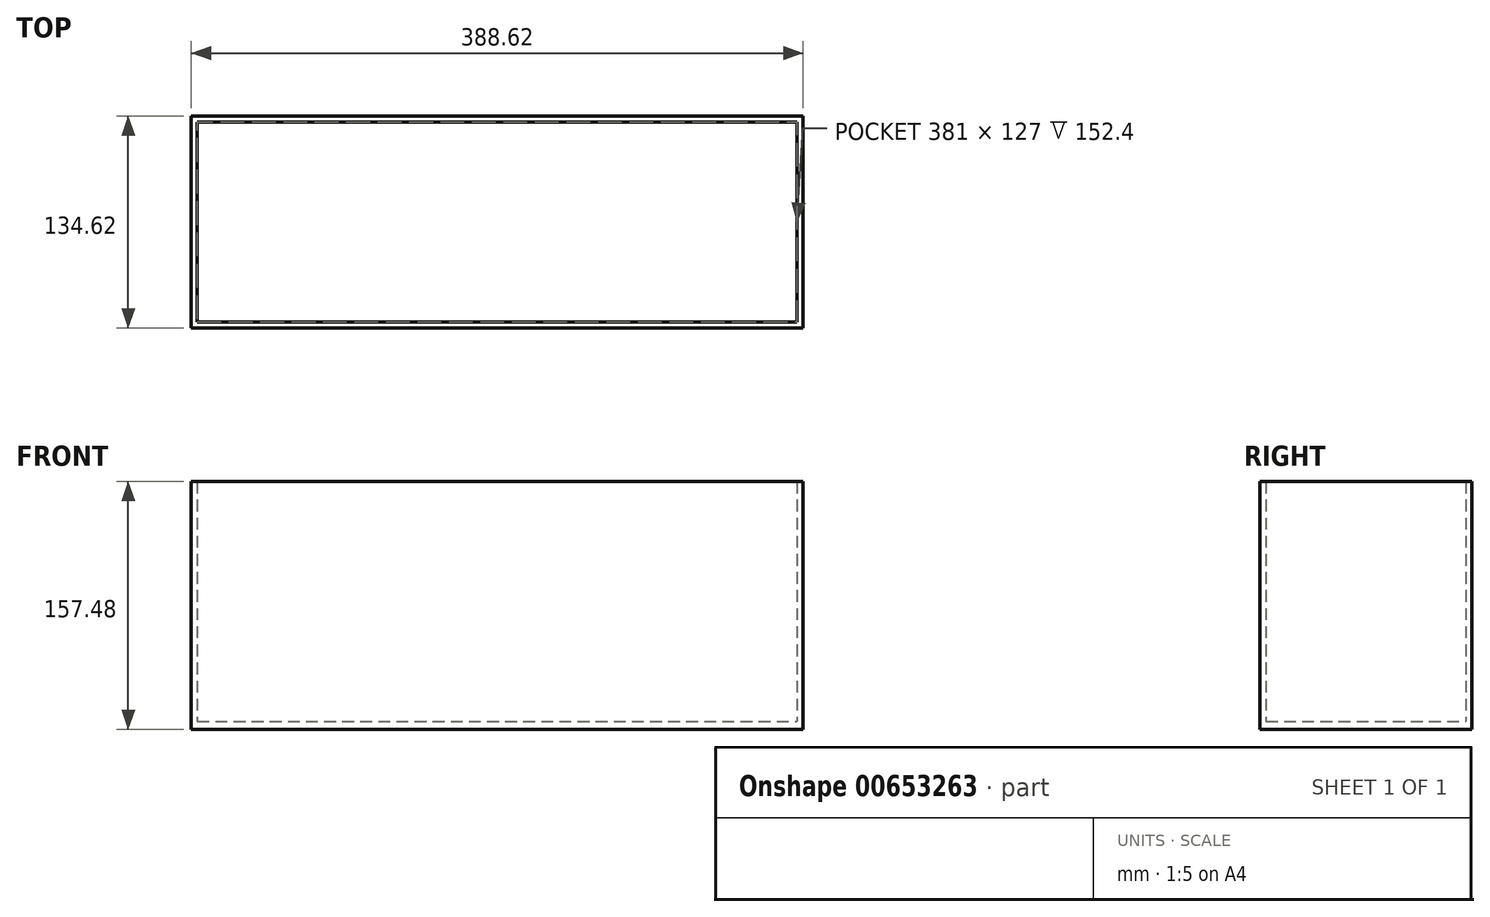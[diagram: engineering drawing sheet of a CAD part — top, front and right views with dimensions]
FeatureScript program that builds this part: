
annotation { "Feature Type Name" : "Feature", "Feature Type Description" : "" }
export const myFeature = defineFeature(function(context is Context, id is Id, definition is map)
    precondition{}
    {
        {
            var Q0;
            Q0=qCreatedBy(makeId("Front.planeOp"),FACE);
            var sketch = newSketch(context, id + "F0", { "sketchPlane" : qUnion([Q0])});
            skLineSegment(sketch, "E0.bottom", {"start": v(-190.5, 76.2) * mm, "end": v(190.5, 76.2) * mm});
            skLineSegment(sketch, "E0.top", {"start": v(-190.5, -76.2) * mm, "end": v(190.5, -76.2) * mm});
            skLineSegment(sketch, "E0.left", {"start": v(-190.5, 76.2) * mm, "end": v(-190.5, -76.2) * mm});
            skLineSegment(sketch, "E0.right", {"start": v(190.5, 76.2) * mm, "end": v(190.5, -76.2) * mm});
            skPoint(sketch, "E0.middle", {"position": v(0, 0) * mm});
            skSolve(sketch);
        }
        {
            var Q0;
            Q0 = qSketchRegion(id + "F0", true);
            var Q1;
            Q1=makeQuery(id+"F0.imprint","IMPRINT",FACE,{"disambiguationData":[TD([[makeQuery(id+"F0.imprint","IMPRINT",EDGE,{"derivedFrom":sQuery(id+"F0.wireOp",EDGE,"E0.bottom")}),-1.0]])]});
            extrude(context, id + "F1", {"entities" : qUnion([Q0, Q1]), "depth" : 25.4 * mm, "offsetDistance" : 25.4 * mm});
        }
        {
            var Q0;
            Q0=makeQuery(id+"F1.opExtrude","CAP_FACE",FACE,{"disambiguationData":[OSD([sQuery(id+"F0.wireOp",EDGE,"E0.bottom"),sQuery(id+"F0.wireOp",EDGE,"E0.top"),sQuery(id+"F0.wireOp",EDGE,"E0.left"),sQuery(id+"F0.wireOp",EDGE,"E0.right")])],"isStart":false});
            extrude(context, id + "F2", {"entities" : qUnion([Q0]), "operationType" : NewBodyOperationType.ADD, "depth" : 101.6 * mm, "offsetDistance" : 25.4 * mm});
        }
        {
            var Q0;
            {var subQ0=sQuery(id+"F0.wireOp",EDGE,"E0.bottom");Q0=makeQuery(id+"F2.boolean.opBoolean","MERGE",FACE,{"derivedFrom":[makeQuery(id+"F1.opExtrude","SWEPT_FACE",FACE,{"disambiguationData":[OSD([subQ0])]}),makeQuery(id+"F2.opExtrude","SWEPT_FACE",FACE,{"disambiguationData":[OSD([subQ0])]})]});}
            shell(context, id + "F3", {"entities" : qUnion([Q0]), "thickness" : 2.54 * mm, "oppositeDirection" : true});
        }
        {
            var Q0;
            Q0=makeQuery(id+"F2.opExtrude","CAP_FACE",FACE,{"disambiguationData":[OSD([sQuery(id+"F0.wireOp",EDGE,"E0.bottom"),sQuery(id+"F0.wireOp",EDGE,"E0.top"),sQuery(id+"F0.wireOp",EDGE,"E0.left"),sQuery(id+"F0.wireOp",EDGE,"E0.right")])],"isStart":false});
            extrude(context, id + "F4", {"entities" : qUnion([Q0]), "operationType" : NewBodyOperationType.ADD, "depth" : 1.27 * mm, "offsetDistance" : 25.4 * mm});
        }
        {
            var Q0;
            {var subQ0=sQuery(id+"F0.wireOp",EDGE,"E0.right");Q0=makeQuery(id+"F4.boolean.opBoolean","MERGE",FACE,{"derivedFrom":[makeQuery(id+"F2.boolean.opBoolean","MERGE",FACE,{"derivedFrom":[makeQuery(id+"F1.opExtrude","SWEPT_FACE",FACE,{"disambiguationData":[OSD([subQ0])]}),makeQuery(id+"F2.opExtrude","SWEPT_FACE",FACE,{"disambiguationData":[OSD([subQ0])]})]}),makeQuery(id+"F4.opExtrude","SWEPT_FACE",FACE,{"disambiguationData":[OSD([subQ0])]})]});}
            extrude(context, id + "F5", {"entities" : qUnion([Q0]), "operationType" : NewBodyOperationType.ADD, "depth" : 1.27 * mm, "offsetDistance" : 25.4 * mm});
        }
        {
            var Q0;
            {var subQ0=sQuery(id+"F0.wireOp",EDGE,"E0.right");Q0=makeQuery(id+"F5.boolean.opBoolean","MERGE",FACE,{"derivedFrom":[makeQuery(id+"F1.opExtrude","CAP_FACE",FACE,{"disambiguationData":[OSD([sQuery(id+"F0.wireOp",EDGE,"E0.bottom"),sQuery(id+"F0.wireOp",EDGE,"E0.top"),sQuery(id+"F0.wireOp",EDGE,"E0.left"),subQ0])],"isStart":true}),makeQuery(id+"F5.opExtrude","SWEPT_FACE",FACE,{"disambiguationData":[OSD([subQ0]),TDD([makeQuery(id+"F1.opExtrude","CAP_EDGE",EDGE,{"disambiguationData":[OSD([subQ0])],"isStart":true})])]})]});}
            extrude(context, id + "F6", {"entities" : qUnion([Q0]), "operationType" : NewBodyOperationType.ADD, "depth" : 1.27 * mm, "offsetDistance" : 25.4 * mm});
        }
        {
            var Q0;
            {var subQ0=sQuery(id+"F0.wireOp",EDGE,"E0.left");Q0=makeQuery(id+"F6.boolean.opBoolean","MERGE",FACE,{"derivedFrom":[makeQuery(id+"F4.boolean.opBoolean","MERGE",FACE,{"derivedFrom":[makeQuery(id+"F2.boolean.opBoolean","MERGE",FACE,{"derivedFrom":[makeQuery(id+"F1.opExtrude","SWEPT_FACE",FACE,{"disambiguationData":[OSD([subQ0])]}),makeQuery(id+"F2.opExtrude","SWEPT_FACE",FACE,{"disambiguationData":[OSD([subQ0])]})]}),makeQuery(id+"F4.opExtrude","SWEPT_FACE",FACE,{"disambiguationData":[OSD([subQ0])]})]}),makeQuery(id+"F6.opExtrude","SWEPT_FACE",FACE,{"disambiguationData":[OSD([subQ0])]})]});}
            extrude(context, id + "F7", {"entities" : qUnion([Q0]), "operationType" : NewBodyOperationType.ADD, "depth" : 1.27 * mm, "offsetDistance" : 25.4 * mm});
        }
        {
            var Q0;
            {var subQ0=sQuery(id+"F0.wireOp",EDGE,"E0.top");var subQ1=sQuery(id+"F0.wireOp",EDGE,"E0.right");Q0=makeQuery(id+"F7.boolean.opBoolean","MERGE",FACE,{"derivedFrom":[makeQuery(id+"F6.boolean.opBoolean","MERGE",FACE,{"derivedFrom":[makeQuery(id+"F5.boolean.opBoolean","MERGE",FACE,{"derivedFrom":[makeQuery(id+"F4.boolean.opBoolean","MERGE",FACE,{"derivedFrom":[makeQuery(id+"F2.boolean.opBoolean","MERGE",FACE,{"derivedFrom":[makeQuery(id+"F1.opExtrude","SWEPT_FACE",FACE,{"disambiguationData":[OSD([subQ0])]}),makeQuery(id+"F2.opExtrude","SWEPT_FACE",FACE,{"disambiguationData":[OSD([subQ0])]})]}),makeQuery(id+"F4.opExtrude","SWEPT_FACE",FACE,{"disambiguationData":[OSD([subQ0])]})]}),makeQuery(id+"F5.opExtrude","SWEPT_FACE",FACE,{"disambiguationData":[OSD([subQ0,subQ1])]})]}),makeQuery(id+"F6.opExtrude","SWEPT_FACE",FACE,{"disambiguationData":[OSD([subQ0,subQ1])]})]}),makeQuery(id+"F7.opExtrude","SWEPT_FACE",FACE,{"disambiguationData":[OSD([subQ0,sQuery(id+"F0.wireOp",EDGE,"E0.left")])]})]});}
            extrude(context, id + "F8", {"entities" : qUnion([Q0]), "operationType" : NewBodyOperationType.ADD, "depth" : 2.54 * mm, "offsetDistance" : 25.4 * mm});
        }
    });
